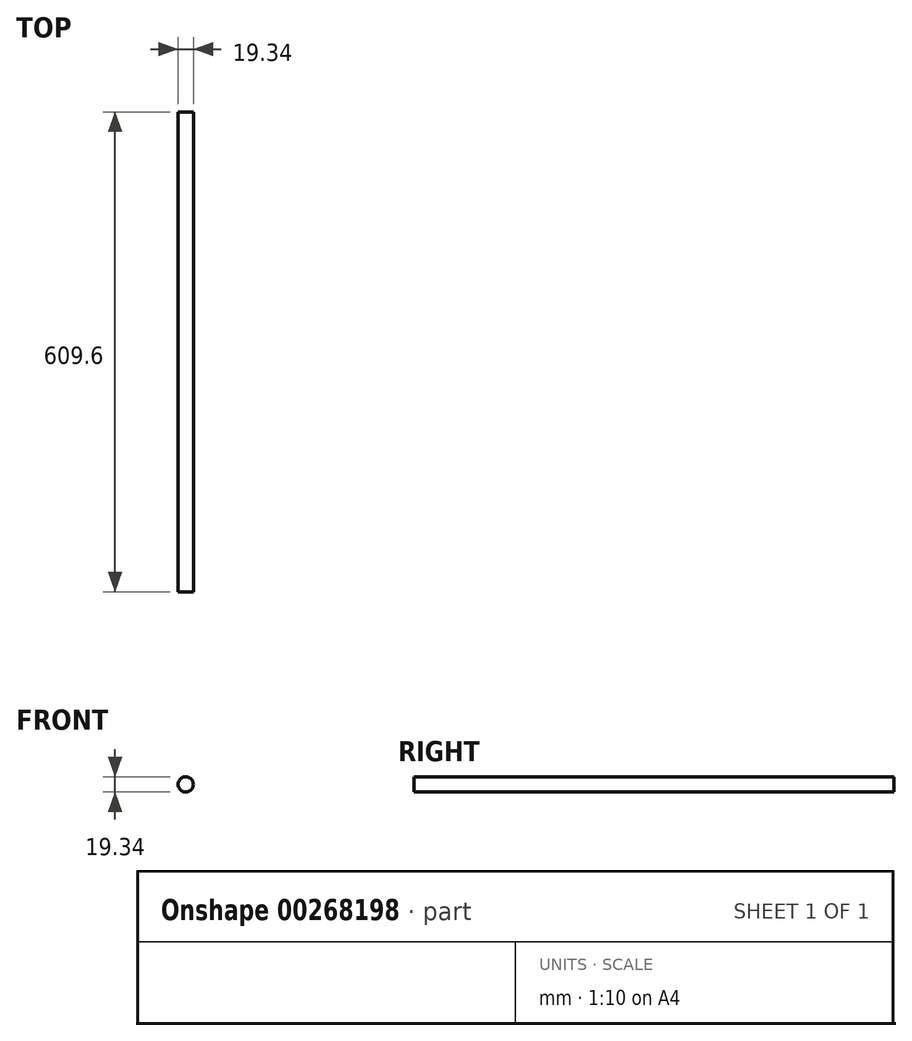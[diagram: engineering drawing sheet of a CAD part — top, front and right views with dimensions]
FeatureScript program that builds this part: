
annotation { "Feature Type Name" : "Feature", "Feature Type Description" : "" }
export const myFeature = defineFeature(function(context is Context, id is Id, definition is map)
    precondition{}
    {
        {
            var Q0;
            Q0=qCreatedBy(makeId("Front.planeOp"),FACE);
            var sketch = newSketch(context, id + "F0", { "sketchPlane" : qUnion([Q0])});
            skPoint(sketch, "E0", {"position": v(0, 0) * mm});
            skCircle(sketch, "E1", {"center": v(0, 0) * mm, "radius": 9.67 * mm});
            skSolve(sketch);
        }
        {
            var Q0;
            Q0 = qSketchRegion(id + "F0", true);
            extrude(context, id + "F1", {"entities" : qUnion([Q0]), "depth" : 609.6 * mm});
        }
    });
